# Revit family: Domotics-DomesticRanges-GEWISS-SYSTEM_COMMAND-TWO-WAY_SWITCH
name_source: partatom
category: Apparecchi elettrici
revit_build: Autodesk Revit 2016 (Build: 20161004_0715(x64)
units: mm (PartAtom-declared; Revit-internal decimal feet)

## family parameters
Condiviso = Sì
Host = Superficie
Mantenere orientamento annotazione = Sì
Numero OmniClass = 23.80.50.11.14
Punto di calcolo locali = Sì
Quota connettore circolare = Usa diametro
Taglio con vuoti quando caricato = No
Tipo di parte = Normale
Titolo OmniClass = Switches

## types (6) — shared parameters
Carico apparente = 0 VA
Catalogue = DOMOTICS
Catalogue Range = SYSTEM - DOMESTIC RANGE
Characteristics = 1P - 16AX
Description. = Two-way switch
Electrocod = 0130
IDF = f2f82db9-438a-4ea3-ba1b-6537c92e0f9d
IDT = 9688a8e7-36e3-4dc0-80d2-983e6bf9a2f0
Immagine tipo = GW21588.jpg
N. poli = 1
No. SYSTEM modules = 1
Produttore = GEWISS S.p.A.
Prospetto di default = 1219 mm
Pulsante = GEWISS NERO
SEO = 2 way switch
Simbolo_ = SIMBOLO DEVIATORI : DEV1PLUM
Technical sheet = https://www.gewiss.com
Tipo_ = SYSTEM DEVIATORI_BASE : GW20588 - DEVIATORE 1P 16AX ILLUMINABILE SY/WT
URL = https://www.gewiss.com
Version file RFA = 19.4
Vetro illuminato = Sì
Volt = 230 V
Voltage = 250 V ac
Voltage: = 250 V ac

## per-type parameters (varying)
| type | Button key | Colour | Description: | Descrizione | EAN code | Modello | Type | Typology |
| GW20576 - 2-way switch-1P 16Ax white | Neutral | White | 1P - 16AX | 2-WAY SWITCH-1P 16AX SY/WT | 8011564132955 | GW20576 | General | General |
| GW21588 - 2-way switch-1P 16Ax illuminable black | With replaceable neutral lens | Black | 1P - 16AX illuminable | 2-WAY SWITCH-1P 16AX ILLUMINABLE SY/BK | 8011564133068 | GW21588 | Illuminable | Illuminable |
| GW20588 - 2-way switch-1P 16Ax illuminable white | With replaceable neutral lens | White | 1P - 16AX illuminable | 2-WAY SWITCH-1P 16AX ILLUMINABLE SY/WT | 8011564132979 | GW20588 | Illuminable | Illuminable |
| GW21577 - 2-way switch-1P 16Ax luminous 230V black | With replaceable neutral lens | Black | 1P - 16 AX backlit | 2-WAY SWITCH-1P 16AX LUMINOUS 230V SY/BK | 8011564133051 | GW21577 | Backlit 230V ac (0.4W) | Backlit 230V ac (0.4W) |
| GW20577 - 2-way switch-1P 16Ax luminous 230V white | With replaceable neutral lens | White | 1P - 16 AX backlit | 2-WAY SWITCH-1P 16AX LUMINOUS 230V SY/WT | 8011564132962 | GW20577 | Backlit 230V ac (0.4W) | Backlit 230V ac (0.4W) |
| GW21576 - 2-way switch-1P 16Ax black | Neutral | Black | 1P - 16AX | 2-WAY SWITCH-1P 16AX SY/BK | 8011564133044 | GW21576 | General | General |

## geometry (parser evidence)
native form markers: Sweep x1
no freeform markers — native parametric forms only
